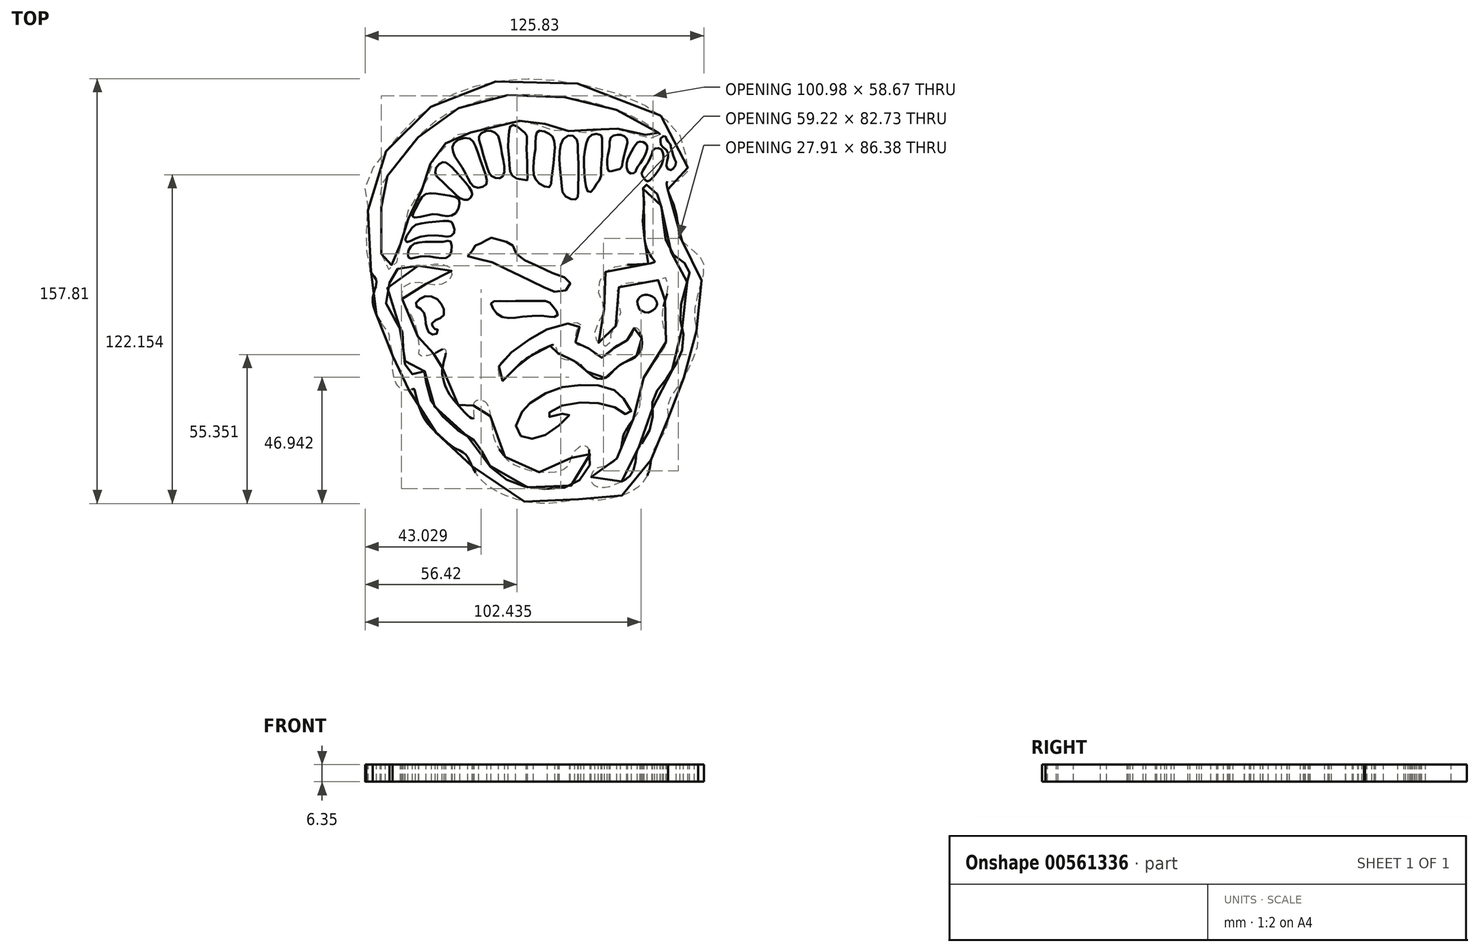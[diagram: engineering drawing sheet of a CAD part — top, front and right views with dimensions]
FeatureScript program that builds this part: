
annotation { "Feature Type Name" : "Feature", "Feature Type Description" : "" }
export const myFeature = defineFeature(function(context is Context, id is Id, definition is map)
    precondition{}
    {
        {
            var Q0;
            Q0=qCreatedBy(makeId("Top.planeOp"),FACE);
            var sketch = newSketch(context, id + "F0", { "sketchPlane" : qUnion([Q0])});
            skFitSpline(sketch, "E0", {"points": [v(57.34, 19.53) * mm, v(62.96, 14.6) * mm, v(65.23, 11.51) * mm, v(65.1, 6.78) * mm, v(63.4, 0.47) * mm, v(62.01, -6.29) * mm, v(62.2, -11.34) * mm, v(63.15, -16.32) * mm, v(62.96, -19.92) * mm, v(60.37, -26.55) * mm, v(57.34, -32.42) * mm, v(54.19, -36.9) * mm, v(51.85, -41.58) * mm, v(52.1, -45.11) * mm, v(51.79, -48.9) * mm, v(50.34, -52.24) * mm, v(46.61, -58.37) * mm, v(45.8, -61.9) * mm, v(44.84, -66.64) * mm, v(41.94, -71.18) * mm, v(36.83, -74.46) * mm, v(29.95, -76.36) * mm, v(24.45, -76.86) * mm, v(21.55, -76.17) * mm, v(19.21, -76.42) * mm, v(15.55, -77.12) * mm, v(11, -77.75) * mm, v(1.73, -77.87) * mm, v(-11.34, -73.7) * mm, v(-18.1, -68.47) * mm, v(-21.38, -62.85) * mm, v(-23.27, -59.63) * mm, v(-27.18, -57.42) * mm, v(-33.56, -52.18) * mm, v(-39.3, -44.92) * mm, v(-42.2, -35.52) * mm, v(-42.33, -35.45) * mm, v(-44.16, -36.02) * mm, v(-47.45, -35.2) * mm, v(-49.34, -32.42) * mm, v(-50.29, -26.49) * mm, v(-50.16, -22.57) * mm, v(-51.42, -17.4) * mm, v(-51.42, -15.44) * mm, v(-54.96, -10.26) * mm, v(-57.04, -5.85) * mm, v(-57.48, -1.17) * mm, v(-56.28, 4.5) * mm, v(-58.18, 7.85) * mm, v(-59.7, 15.05) * mm, v(-59.95, 22.3) * mm, v(-59.44, 34.18) * mm, v(-60.26, 40.87) * mm, v(-53.82, 51.28) * mm, v(-48.65, 57.6) * mm, v(-42.52, 64.22) * mm, v(-33.69, 70.73) * mm, v(-24.6, 75.27) * mm, v(-12.54, 78.55) * mm, v(1.8, 79.7) * mm, v(18.4, 77.92) * mm, v(39.16, 72.05) * mm, v(51.1, 64.67) * mm, v(56.9, 57.85) * mm, v(59.1, 48.95) * mm, v(59.3, 45.16) * mm, v(56.71, 42.07) * mm, v(54.31, 41.56) * mm, v(51.91, 41.69) * mm, v(52.1, 38.22) * mm, v(54.5, 31.84) * mm, v(56.02, 23.82) * mm, v(57.34, 19.53) * mm]});
            skSolve(sketch);
        }
        {
            var Q0;
            Q0 = qSketchRegion(id + "F0", true);
            extrude(context, id + "F1", {"entities" : qUnion([Q0]), "oppositeDirection" : true, "depth" : 6.35 * mm, "offsetDistance" : 25.4 * mm});
        }
        {
            var Q0;
            Q0=qCreatedBy(makeId("Top.planeOp"),FACE);
            var sketch = newSketch(context, id + "F2", { "sketchPlane" : qUnion([Q0])});
            skFitSpline(sketch, "E1", {"points": [v(-27.86, 37.73) * mm, v(-24.64, 35.15) * mm, v(-22.36, 34.68) * mm, v(-20.83, 36.15) * mm, v(-20.77, 37.61) * mm, v(-23.18, 41.13) * mm, v(-28.27, 46.87) * mm, v(-30.09, 48.4) * mm, v(-31.5, 48.74) * mm, v(-34.01, 46.75) * mm, v(-34.13, 44) * mm, v(-32.96, 42.65) * mm, v(-27.86, 37.73) * mm]});
            skFitSpline(sketch, "E2", {"points": [v(-23, 44.4) * mm, v(-21.71, 41.6) * mm, v(-20.01, 39.6) * mm, v(-17.73, 39.25) * mm, v(-15.62, 40.2) * mm, v(-15.15, 41.89) * mm, v(-16.67, 46.87) * mm, v(-18.78, 53.02) * mm, v(-20.36, 56.48) * mm, v(-22.47, 57.77) * mm, v(-26.46, 56.71) * mm, v(-27.92, 54.54) * mm, v(-27.69, 52.32) * mm, v(-26.16, 49.33) * mm, v(-23, 44.4) * mm]});
            skFitSpline(sketch, "E3", {"points": [v(-17.55, 55.3) * mm, v(-18.25, 57.77) * mm, v(-17.26, 59.46) * mm, v(-14.39, 60.4) * mm, v(-11.7, 59.35) * mm, v(-10.4, 56.6) * mm, v(-9.35, 50.91) * mm, v(-8.65, 45.81) * mm, v(-9.64, 43.12) * mm, v(-11.28, 42.7) * mm, v(-13.8, 43.88) * mm, v(-14.86, 46.17) * mm, v(-16.67, 51.97) * mm, v(-17.55, 55.3) * mm]});
            skFitSpline(sketch, "E4", {"points": [v(-7.36, 54.49) * mm, v(-6.89, 60.17) * mm, v(-6.36, 62.22) * mm, v(-4.84, 62.51) * mm, v(-3.08, 61.28) * mm, v(-1.32, 59.82) * mm, v(-0.33, 58.53) * mm, v(-0.5, 54.9) * mm, v(-0.21, 50.2) * mm, v(-0.15, 44.76) * mm, v(-0.1, 42.07) * mm, v(-0.62, 42.07) * mm, v(-4.02, 42.65) * mm, v(-6.07, 44.17) * mm, v(-6.71, 46.87) * mm, v(-7.12, 52.2) * mm, v(-7.36, 54.49) * mm]});
            skFitSpline(sketch, "E5", {"points": [v(2.2, 49.1) * mm, v(2.78, 53.14) * mm, v(2.95, 57.41) * mm, v(3.42, 59.82) * mm, v(4.53, 60.46) * mm, v(7.23, 59.58) * mm, v(9.1, 58.23) * mm, v(9.98, 55.36) * mm, v(9.63, 48.98) * mm, v(8.87, 42.53) * mm, v(8.46, 39.84) * mm, v(6.7, 39.49) * mm, v(3.71, 41.36) * mm, v(2.3, 43.88) * mm, v(2.2, 49.1) * mm]});
            skFitSpline(sketch, "E6", {"points": [v(12.38, 42.65) * mm, v(11.8, 49.8) * mm, v(12.15, 54.37) * mm, v(13.03, 56.95) * mm, v(15.43, 58.7) * mm, v(17.13, 58.3) * mm, v(18.42, 56.6) * mm, v(18.65, 54.6) * mm, v(18.65, 51.09) * mm, v(18.83, 47.63) * mm, v(18.89, 43.94) * mm, v(18.71, 40.13) * mm, v(18.65, 36.68) * mm, v(18.36, 35.27) * mm, v(17.42, 34.8) * mm, v(15.9, 35.04) * mm, v(13.38, 36.68) * mm, v(12.74, 38.55) * mm, v(12.38, 42.65) * mm]});
            skFitSpline(sketch, "E7", {"points": [v(25.62, 40.72) * mm, v(23.75, 37.79) * mm, v(22.4, 37.73) * mm, v(21.46, 40.72) * mm, v(20.88, 47.75) * mm, v(21.4, 54.3) * mm, v(22.87, 58.18) * mm, v(24.86, 59.23) * mm, v(27.44, 58.59) * mm, v(27.62, 56.83) * mm, v(27.67, 52.38) * mm, v(27.26, 46.87) * mm, v(26.97, 42.6) * mm, v(25.62, 40.72) * mm]});
            skFitSpline(sketch, "E8", {"points": [v(29.78, 51.44) * mm, v(29.55, 48.1) * mm, v(30.2, 45.35) * mm, v(31.83, 45.58) * mm, v(34.53, 46.4) * mm, v(35.35, 48.98) * mm, v(36.46, 53.78) * mm, v(36.99, 57) * mm, v(35.17, 58.64) * mm, v(33.06, 58.88) * mm, v(30.84, 57.82) * mm, v(30.37, 54.78) * mm, v(29.78, 51.44) * mm]});
            skFitSpline(sketch, "E9", {"points": [v(36.76, 48.28) * mm, v(38.51, 52.61) * mm, v(40.45, 55.72) * mm, v(42.09, 56.36) * mm, v(44.14, 55.19) * mm, v(44.25, 53.37) * mm, v(42.79, 49.74) * mm, v(40.45, 46.4) * mm, v(39.8, 44.88) * mm, v(37.87, 44.64) * mm, v(36.76, 48.28) * mm]});
            skFitSpline(sketch, "E10", {"points": [v(43.08, 42.89) * mm, v(42.26, 44.35) * mm, v(43.5, 46.87) * mm, v(45.95, 51.26) * mm, v(46.83, 53.55) * mm, v(49.23, 53.72) * mm, v(50.4, 51.09) * mm, v(49.94, 48.22) * mm, v(48.06, 45) * mm, v(45.66, 42.24) * mm, v(44.2, 41.6) * mm, v(43.08, 42.89) * mm]});
            skFitSpline(sketch, "E11", {"points": [v(-41.16, 32.22) * mm, v(-39.64, 35.33) * mm, v(-37.18, 37.09) * mm, v(-33.49, 36.91) * mm, v(-28.16, 36.09) * mm, v(-25.58, 34.86) * mm, v(-25.34, 33.16) * mm, v(-26.8, 29.76) * mm, v(-28.98, 28.7) * mm, v(-31.79, 28.94) * mm, v(-34.6, 29.41) * mm, v(-39.23, 28.53) * mm, v(-42.45, 28.24) * mm, v(-42.86, 28.83) * mm, v(-41.16, 32.22) * mm]});
            skFitSpline(sketch, "E12", {"points": [v(-44.03, 22.85) * mm, v(-45.5, 20.21) * mm, v(-45.03, 19.04) * mm, v(-42.68, 19.86) * mm, v(-38.88, 21.15) * mm, v(-31.67, 21.33) * mm, v(-29.1, 21.1) * mm, v(-27.22, 22.62) * mm, v(-27.63, 24.84) * mm, v(-28.33, 26.54) * mm, v(-30.38, 26.9) * mm, v(-36.77, 26.3) * mm, v(-41.98, 25.2) * mm, v(-44.03, 22.85) * mm]});
            skFitSpline(sketch, "E13", {"points": [v(-44.2, 16.11) * mm, v(-42.74, 18.1) * mm, v(-39.81, 18.98) * mm, v(-34.54, 19.16) * mm, v(-30.67, 19.28) * mm, v(-28.92, 19.45) * mm, v(-28.21, 17) * mm, v(-29.15, 13.89) * mm, v(-31.08, 13.07) * mm, v(-35.13, 13.48) * mm, v(-38.88, 13.77) * mm, v(-41.86, 13.18) * mm, v(-44.03, 13.07) * mm, v(-44.56, 14.12) * mm, v(-44.2, 16.11) * mm]});
            skFitSpline(sketch, "E14", {"points": [v(-40.75, 10.2) * mm, v(-36.42, 10.66) * mm, v(-32.37, 10.84) * mm, v(-28.92, 9.67) * mm, v(-28.39, 5.92) * mm, v(-30.73, 3.75) * mm, v(-34.37, 3.05) * mm, v(-38, 3.58) * mm, v(-42.04, 3.99) * mm, v(-46.02, 2.58) * mm, v(-46.96, -0.58) * mm, v(-45.73, -4.27) * mm, v(-43.27, -8.37) * mm, v(-41.63, -12.36) * mm, v(-40.46, -20.38) * mm, v(-40.46, -22.79) * mm, v(-39.81, -23.14) * mm, v(-37, -23.08) * mm, v(-33.84, -21.9) * mm, v(-31.79, -20.85) * mm, v(-30.8, -20.74) * mm, v(-30.44, -22.02) * mm, v(-31.73, -28.12) * mm, v(-31.2, -32.69) * mm, v(-29.39, -36.96) * mm, v(-25.52, -41.88) * mm, v(-21.3, -46.16) * mm, v(-20.13, -46.45) * mm, v(-19.9, -46.04) * mm, v(-20.13, -42.47) * mm, v(-19.72, -40.3) * mm, v(-18.02, -39.54) * mm, v(-15.56, -40.6) * mm, v(-14.27, -43.47) * mm, v(-13.28, -49.8) * mm, v(-12.1, -55.18) * mm, v(-9.06, -60.05) * mm, v(-6.07, -63.03) * mm, v(-1.8, -64.9) * mm, v(2.25, -66.14) * mm, v(8.28, -66.49) * mm, v(12.97, -65.55) * mm, v(15.43, -63.33) * mm, v(16.78, -59.58) * mm, v(18.95, -57.18) * mm, v(20.35, -56.41) * mm, v(22.58, -57.59) * mm, v(23.16, -60.7) * mm, v(22.75, -64.85) * mm, v(19.41, -69.24) * mm, v(15.6, -71.65) * mm, v(10.74, -72.52) * mm, v(4, -72.7) * mm, v(-1.91, -71.65) * mm, v(-7.24, -69.6) * mm, v(-12.92, -65.5) * mm, v(-15.74, -61.63) * mm, v(-17.84, -56.88) * mm, v(-19.08, -55.18) * mm, v(-23.23, -52.78) * mm, v(-28.27, -48.86) * mm, v(-32.78, -44.4) * mm, v(-35.95, -39.95) * mm, v(-37.76, -33.86) * mm, v(-37.82, -29.93) * mm, v(-38.11, -29.05) * mm, v(-39.05, -29.11) * mm, v(-41.4, -29.76) * mm, v(-43.91, -29.93) * mm, v(-45.5, -27.36) * mm, v(-45.61, -23.26) * mm, v(-46.43, -18.69) * mm, v(-46.32, -15.46) * mm, v(-47.6, -12.3) * mm, v(-50.18, -8.5) * mm, v(-52.53, -4.45) * mm, v(-52.12, 2.17) * mm, v(-49.36, 7.44) * mm, v(-48.02, 9.32) * mm, v(-40.75, 10.2) * mm]});
            skFitSpline(sketch, "E15", {"points": [v(-54.46, 14.7) * mm, v(-53.7, 10.49) * mm, v(-51.76, 8.85) * mm, v(-51.18, 9.02) * mm, v(-50.77, 10.25) * mm, v(-49.6, 11.07) * mm, v(-48.07, 12.25) * mm, v(-47.02, 15.35) * mm, v(-47.25, 17.87) * mm, v(-47.2, 20.86) * mm, v(-46.38, 23.03) * mm, v(-44.97, 24.9) * mm, v(-44.38, 29.59) * mm, v(-43.91, 32.99) * mm, v(-40.75, 36.97) * mm, v(-38.35, 39.2) * mm, v(-37.35, 41.07) * mm, v(-37, 45.81) * mm, v(-35.54, 48.98) * mm, v(-33.37, 50.91) * mm, v(-31.26, 52.61) * mm, v(-30.8, 55.13) * mm, v(-28.62, 57.53) * mm, v(-25.4, 59.35) * mm, v(-22.53, 59.76) * mm, v(-20.01, 60) * mm, v(-18.6, 60.99) * mm, v(-15.1, 62.1) * mm, v(-12.1, 61.98) * mm, v(-10.23, 62.1) * mm, v(-7.89, 63.57) * mm, v(-6.36, 64.21) * mm, v(-2.73, 64.03) * mm, v(-1.2, 63.21) * mm, v(1.6, 62.51) * mm, v(4.89, 62.92) * mm, v(7.64, 62.45) * mm, v(9.63, 60.28) * mm, v(11.5, 59.64) * mm, v(15.2, 60.28) * mm, v(17.19, 60.17) * mm, v(19.65, 59.7) * mm, v(22.23, 59.93) * mm, v(24.8, 61.05) * mm, v(27.56, 60.93) * mm, v(29.37, 60.28) * mm, v(32.07, 60.87) * mm, v(34.88, 61.1) * mm, v(38.34, 59.76) * mm, v(41.15, 58.88) * mm, v(44.72, 58.7) * mm, v(46.3, 57.36) * mm, v(47.48, 57) * mm, v(48.88, 58.35) * mm, v(49.12, 59) * mm, v(43.6, 63.21) * mm, v(35.17, 67.32) * mm, v(24.86, 70.6) * mm, v(13.61, 72.82) * mm, v(-0.04, 73.82) * mm, v(-11.64, 73.11) * mm, v(-21.36, 70.36) * mm, v(-31.2, 66.08) * mm, v(-39.11, 59.64) * mm, v(-44.5, 53.84) * mm, v(-51.3, 44.64) * mm, v(-54.23, 40.6) * mm, v(-54.81, 36.03) * mm, v(-54.4, 31.81) * mm, v(-54.64, 22.2) * mm, v(-54.46, 14.7) * mm]});
            skFitSpline(sketch, "E16", {"points": [v(51.75, 48.98) * mm, v(52.26, 51.54) * mm, v(51.3, 53.4) * mm, v(49.71, 54.74) * mm, v(49.32, 56.44) * mm, v(49.44, 57.7) * mm, v(50.82, 58.48) * mm, v(51.39, 58) * mm, v(51.75, 56.86) * mm, v(52.97, 55.37) * mm, v(53.4, 53.48) * mm, v(53.96, 51.54) * mm, v(54.83, 49.32) * mm, v(55.16, 48.34) * mm, v(53.9, 46.15) * mm, v(53.06, 45.73) * mm, v(51.69, 46.6) * mm, v(51.75, 48.98) * mm]});
            skFitSpline(sketch, "E17", {"points": [v(43.35, 20.43) * mm, v(42.79, 26.7) * mm, v(43.23, 33.08) * mm, v(43.01, 38.32) * mm, v(42.57, 40.53) * mm, v(43.04, 40.71) * mm, v(46.03, 39.22) * mm, v(48.46, 36.14) * mm, v(49.65, 31.87) * mm, v(50.27, 27.32) * mm, v(50.93, 21.3) * mm, v(53.3, 15.3) * mm, v(56.66, 12.55) * mm, v(59.1, 10.25) * mm, v(60.09, 8.32) * mm, v(59.34, 4.33) * mm, v(57.4, -2.18) * mm, v(56.54, -6.98) * mm, v(57.13, -12.18) * mm, v(57.88, -16.23) * mm, v(57.25, -21.6) * mm, v(55.91, -24.83) * mm, v(52.08, -30.97) * mm, v(48.71, -35.18) * mm, v(47.06, -37.73) * mm, v(46.19, -41.75) * mm, v(46.47, -45.84) * mm, v(45.7, -49.67) * mm, v(43.6, -54) * mm, v(40.95, -57.8) * mm, v(40.24, -60.73) * mm, v(39.58, -64.72) * mm, v(37.59, -68.11) * mm, v(33.26, -70.73) * mm, v(28.86, -72.14) * mm, v(25.4, -71.7) * mm, v(23.84, -70.36) * mm, v(23.66, -67.75) * mm, v(25.12, -65.25) * mm, v(26.96, -64.5) * mm, v(29.52, -63.82) * mm, v(32.13, -62.45) * mm, v(34.2, -59.08) * mm, v(35.25, -54.25) * mm, v(35.97, -51.79) * mm, v(39.08, -46.93) * mm, v(41.4, -43.25) * mm, v(41.67, -38.67) * mm, v(42.36, -33.22) * mm, v(44.32, -29.32) * mm, v(47.25, -25.3) * mm, v(49.96, -21.47) * mm, v(51.36, -18.5) * mm, v(50.9, -14.12) * mm, v(50.2, -10.88) * mm, v(50.18, -6.64) * mm, v(51.33, -1.69) * mm, v(52.08, 1) * mm, v(52.11, 4.23) * mm, v(51.64, 5.64) * mm, v(49.62, 5.64) * mm, v(47.62, 4.48) * mm, v(43.66, 3.95) * mm, v(37.5, 3.89) * mm, v(34.69, 3.14) * mm, v(33.23, 1.05) * mm, v(33.29, -1.7) * mm, v(34.47, -6.12) * mm, v(33.38, -11.13) * mm, v(31.2, -14.25) * mm, v(30.39, -17.74) * mm, v(30.7, -18.49) * mm, v(29.7, -19.64) * mm, v(27, -18.92) * mm, v(25.1, -16.68) * mm, v(25.18, -13.6) * mm, v(26.96, -9.6) * mm, v(28.33, -7.11) * mm, v(28.02, -3.87) * mm, v(26.62, -0.67) * mm, v(26.34, 3.04) * mm, v(28.24, 7.25) * mm, v(30.86, 9.21) * mm, v(34.94, 10.37) * mm, v(40.83, 10.71) * mm, v(45.63, 11.15) * mm, v(47.16, 11.65) * mm, v(47.1, 12.02) * mm, v(46.16, 13.2) * mm, v(44.26, 16.63) * mm, v(43.35, 20.43) * mm]});
            skFitSpline(sketch, "E18", {"points": [v(-7.93, 9.02) * mm, v(-13.72, 11.66) * mm, v(-19.88, 12.99) * mm, v(-22.07, 13.58) * mm, v(-22.18, 14.66) * mm, v(-20.72, 15.85) * mm, v(-20.07, 16.74) * mm, v(-19.99, 17.28) * mm, v(-19.02, 17.83) * mm, v(-17.9, 17.88) * mm, v(-17.23, 18.77) * mm, v(-16.67, 19.16) * mm, v(-15.28, 19.72) * mm, v(-14.42, 19.61) * mm, v(-13.8, 20.43) * mm, v(-12.54, 20.8) * mm, v(-10.86, 20) * mm, v(-9.26, 19.16) * mm, v(-7.58, 19.16) * mm, v(-6.12, 18.53) * mm, v(-5.15, 16.72) * mm, v(-4.37, 14.83) * mm, v(-2.53, 13.13) * mm, v(2.1, 10.78) * mm, v(7.65, 8.21) * mm, v(12.5, 6.24) * mm, v(15.12, 5.1) * mm, v(15.8, 3.65) * mm, v(15.17, 1.83) * mm, v(12.79, 0.67) * mm, v(9.19, 0.8) * mm, v(6, 2.3) * mm, v(1.2, 4.56) * mm, v(-2.56, 6.37) * mm, v(-7.93, 9.02) * mm]});
            skFitSpline(sketch, "E19", {"points": [v(-35.34, -12.25) * mm, v(-35.7, -11.63) * mm, v(-35.05, -10.48) * mm, v(-33, -9.39) * mm, v(-31.58, -8.72) * mm, v(-31.07, -6.58) * mm, v(-32.14, -3.88) * mm, v(-34.13, -1.88) * mm, v(-37.21, -1.02) * mm, v(-39.75, -1.84) * mm, v(-41.48, -3.46) * mm, v(-41.56, -4.67) * mm, v(-40.15, -5.58) * mm, v(-38.57, -7.11) * mm, v(-38.1, -9.26) * mm, v(-37.84, -11.51) * mm, v(-37.27, -13.32) * mm, v(-36.61, -14.67) * mm, v(-35.2, -15.37) * mm, v(-33.9, -15.09) * mm, v(-33.43, -13.73) * mm, v(-33.52, -13.26) * mm, v(-34.74, -13.2) * mm, v(-35.34, -12.25) * mm]});
            skFitSpline(sketch, "E20", {"points": [v(-2.61, -52.95) * mm, v(-4.22, -51.02) * mm, v(-4.14, -47.78) * mm, v(-1.95, -43.74) * mm, v(-0.65, -42.1) * mm, v(3.08, -39.14) * mm, v(9.4, -36) * mm, v(14.77, -34.51) * mm, v(21.62, -34.02) * mm, v(27.41, -34.47) * mm, v(32.47, -36.18) * mm, v(34.3, -37.57) * mm, v(37.16, -41.42) * mm, v(38.49, -44.14) * mm, v(37.91, -45.38) * mm, v(36.2, -44.8) * mm, v(34.11, -43.25) * mm, v(29.58, -41.35) * mm, v(23.73, -40.75) * mm, v(17.4, -40.72) * mm, v(11.19, -42.26) * mm, v(8.14, -44.14) * mm, v(7.26, -45.4) * mm, v(7.38, -45.99) * mm, v(8.72, -45.78) * mm, v(12.3, -44.9) * mm, v(15.04, -44.39) * mm, v(15.48, -44.6) * mm, v(14.75, -46.47) * mm, v(11.07, -49.49) * mm, v(6.61, -52.65) * mm, v(2.76, -53.84) * mm, v(-0.24, -54.08) * mm, v(-2.61, -52.95) * mm]});
            skFitSpline(sketch, "E21", {"points": [v(41.47, -5.84) * mm, v(40.72, -3.6) * mm, v(41.67, -1.3) * mm, v(43.98, -0.51) * mm, v(46.24, -1.16) * mm, v(47.69, -2.63) * mm, v(47.96, -4.4) * mm, v(46.72, -6.12) * mm, v(44.33, -7.11) * mm, v(41.67, -6.12) * mm, v(41.47, -5.84) * mm]});
            skFitSpline(sketch, "E22", {"points": [v(-1.93, -8.73) * mm, v(-6.41, -9.22) * mm, v(-10.4, -8.35) * mm, v(-12.92, -5.72) * mm, v(-13.58, -3.55) * mm, v(-12.08, -2.9) * mm, v(-7.63, -2.94) * mm, v(-0.64, -2.8) * mm, v(4.31, -2.9) * mm, v(7.56, -3.1) * mm, v(8.91, -4.3) * mm, v(10.8, -6.87) * mm, v(11.13, -8.19) * mm, v(9.63, -8.81) * mm, v(6.3, -8.44) * mm, v(-1.93, -8.73) * mm]});
            skFitSpline(sketch, "E23", {"points": [v(-4.1, -27.42) * mm, v(-7.44, -30.79) * mm, v(-8.65, -32.21) * mm, v(-9.97, -32.48) * mm, v(-10.76, -30.1) * mm, v(-10.84, -27.5) * mm, v(-10.04, -25.8) * mm, v(-7.97, -23.69) * mm, v(-5.04, -21.1) * mm, v(-1.6, -18.52) * mm, v(1.35, -16.64) * mm, v(3.97, -14.84) * mm, v(7, -13.42) * mm, v(10.76, -12.25) * mm, v(14.35, -11.35) * mm, v(18.84, -10.78) * mm, v(19.66, -10.96) * mm, v(19.35, -12.25) * mm, v(18.02, -13.95) * mm, v(17.46, -16.44) * mm, v(17.83, -18.42) * mm, v(18.9, -19.5) * mm, v(21.22, -19.72) * mm, v(22.9, -20.62) * mm, v(24.53, -22.02) * mm, v(26.4, -23.72) * mm, v(27.83, -23.86) * mm, v(29.5, -22.72) * mm, v(31.42, -21.2) * mm, v(32.23, -20.06) * mm, v(33.64, -19.26) * mm, v(35.36, -18.43) * mm, v(37.5, -16.97) * mm, v(38.64, -15.67) * mm, v(39.27, -14.21) * mm, v(39.62, -12.85) * mm, v(40.56, -12.85) * mm, v(41.41, -14.14) * mm, v(42.27, -16.31) * mm, v(42.41, -19.15) * mm, v(41.67, -21.76) * mm, v(39.16, -24.15) * mm, v(36.17, -25.58) * mm, v(33.89, -26.86) * mm, v(31.74, -28.87) * mm, v(29.65, -30.88) * mm, v(26.73, -31.85) * mm, v(23.97, -30.65) * mm, v(20.96, -28.01) * mm, v(18.97, -25.99) * mm, v(18.2, -25.45) * mm, v(15.1, -24.86) * mm, v(11.87, -23.67) * mm, v(11, -21.59) * mm, v(10.44, -19.49) * mm, v(10.1, -18.92) * mm, v(8.77, -19.32) * mm, v(5.55, -20.7) * mm, v(1.98, -22.75) * mm, v(-1.55, -25.02) * mm, v(-3.5, -26.74) * mm, v(-4.1, -27.42) * mm]});
            skSolve(sketch);
        }
        {
            var Q0;
            Q0 = qSketchRegion(id + "F2", true);
            extrude(context, id + "F3", {"entities" : qUnion([Q0]), "operationType" : NewBodyOperationType.REMOVE, "oppositeDirection" : true, "depth" : 6.35 * mm, "offsetDistance" : 25.4 * mm});
        }
    });
